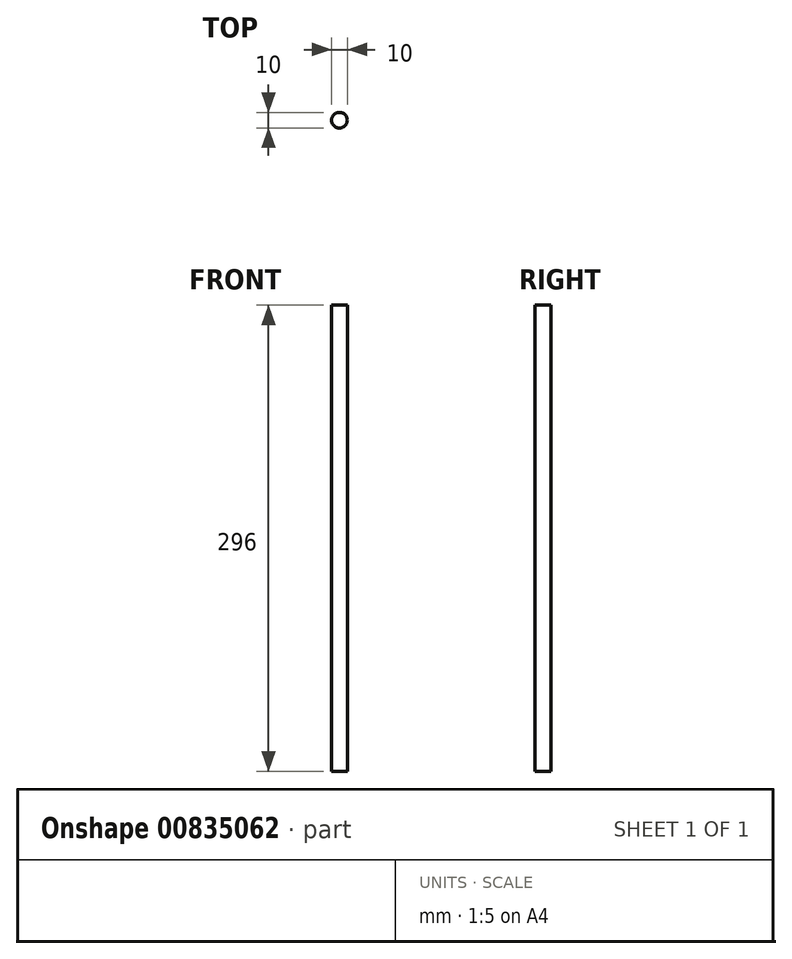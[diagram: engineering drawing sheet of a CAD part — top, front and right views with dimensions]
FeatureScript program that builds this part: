
annotation { "Feature Type Name" : "Feature", "Feature Type Description" : "" }
export const myFeature = defineFeature(function(context is Context, id is Id, definition is map)
    precondition{}
    {
        {
            var Q0;
            Q0=qCreatedBy(makeId("Top.planeOp"),FACE);
            var sketch = newSketch(context, id + "F0", { "sketchPlane" : qUnion([Q0])});
            skCircle(sketch, "E0", {"center": v(0, 0) * mm, "radius": 5 * mm});
            skSolve(sketch);
        }
        {
            var Q0;
            Q0=qSketchRegion(id+"F0",true);
            extrude(context, id + "F1", {"entities" : qUnion([Q0]), "depth" : 296 * mm, "offsetDistance" : 25 * mm});
        }
    });
